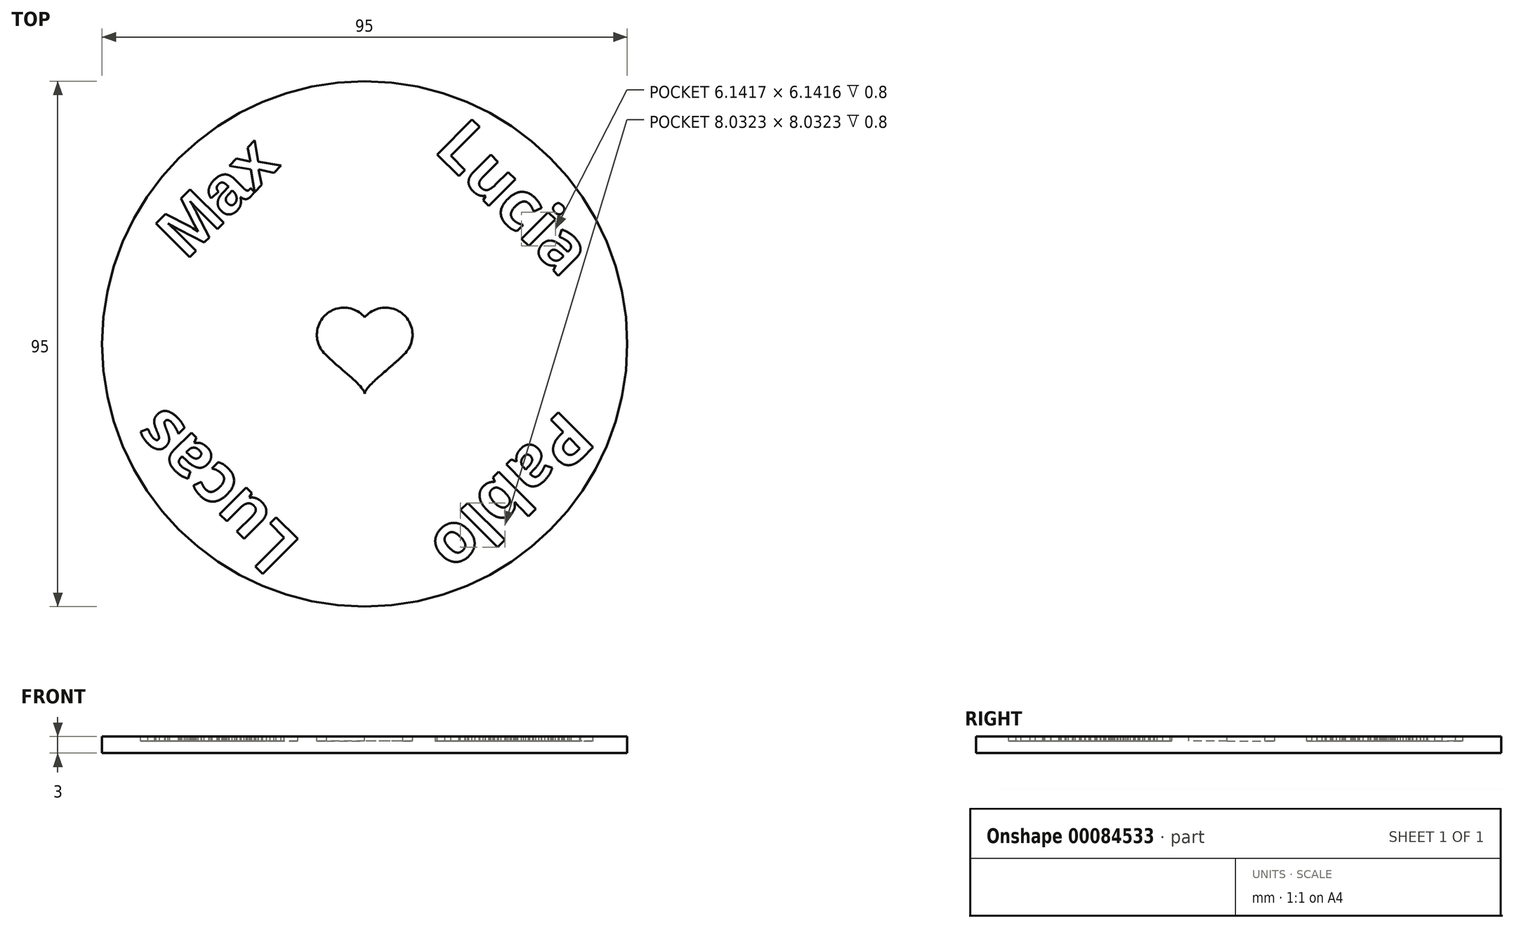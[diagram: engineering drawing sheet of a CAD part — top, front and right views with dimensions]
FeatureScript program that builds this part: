
annotation { "Feature Type Name" : "Feature", "Feature Type Description" : "" }
export const myFeature = defineFeature(function(context is Context, id is Id, definition is map)
    precondition{}
    {
        {
            var Q0;
            Q0=qCreatedBy(makeId("Top.planeOp"),FACE);
            var sketch = newSketch(context, id + "F0", { "sketchPlane" : qUnion([Q0])});
            skCircle(sketch, "E0", {"center": v(0, 0) * mm, "radius": 47.5 * mm});
            skSolve(sketch);
        }
        {
            var Q0;
            Q0 = qSketchRegion(id + "F0", true);
            extrude(context, id + "F1", {"entities" : qUnion([Q0]), "depth" : 3 * mm});
        }
        {
            var Q0;
            Q0=makeQuery(id+"F1.opExtrude","CAP_FACE",FACE,{"disambiguationData":[OSD([sQuery(id+"F0.wireOp",EDGE,"E0")])],"isStart":false});
            var sketch = newSketch(context, id + "F2", { "sketchPlane" : qUnion([Q0])});
            skText(sketch, "E1", { "text": "Max", "fontName": "Arimo-Bold.ttf"});
            skLineSegment(sketch, "E2", {"start": v(0, 0) * mm, "end": v(-47.5, 0) * mm});
            skText(sketch, "E3", { "text": "Lucia", "fontName": "OpenSans-Bold.ttf"});
            skText(sketch, "E4", { "text": "Lucas", "fontName": "OpenSans-Bold.ttf"});
            skLineSegment(sketch, "E5", {"start": v(0, -9) * mm, "end": v(0, 4.8) * mm});
            skPoint(sketch, "E6.startSnap0", {"position": v(0, 0) * mm});
            skArc(sketch, "E7", {"start": v(6.9, -2.1) * mm, "mid": v(7.22, 5.12) * mm, "end": v(0, 4.8) * mm});
            skFitSpline(sketch, "E8", {"points": [v(6.9, -2.1) * mm, v(0, -9) * mm], "startDerivative": vector(-6.9, -6.9) * mm, "endDerivative": vector(0, -3.8) * mm});
            skFitSpline(sketch, "E9.MirrorCS", {"points": [v(-6.9, -2.1) * mm, v(0, -9) * mm], "startDerivative": vector(6.9, -6.9) * mm, "endDerivative": vector(0, -3.8) * mm});
            skArc(sketch, "E10.MirrorCS", {"start": v(-6.9, -2.1) * mm, "mid": v(-7.22, 5.12) * mm, "end": v(0, 4.8) * mm});
            skPoint(sketch, "E11.orphan", {"position": v(-33.59, 33.59) * mm});
            skPoint(sketch, "E12.end.orphan", {"position": v(-33.59, -33.59) * mm});
            skPoint(sketch, "E13.end.orphan", {"position": v(33.59, 33.59) * mm});
            skLineSegment(sketch, "E14", {"start": v(0, 0) * mm, "end": v(4.38, -4.38) * mm});
            skText(sketch, "E15", { "text": "Pablo", "fontName": "OpenSans-Bold.ttf"});
            skPoint(sketch, "E16.orphan", {"position": v(33.59, -33.59) * mm});
            const initialGuessF2  = {"E1": [-0.03225, 0.01512, 0.7071, 0.7071, 0.009], "E3": [0.01233, 0.03505, 0.7071, -0.7071, 0.009], "E4": [-0.01132, -0.03606, -0.7071, 0.7071, 0.009], "E15": [0.03582, -0.01156, -0.7071, -0.7071, 0.009]};
            skSetInitialGuess(sketch, initialGuessF2);
            skSolve(sketch);
        }
        {
            var Q0;
            Q0 = qSketchRegion(id + "F2", true);
            extrude(context, id + "F3", {"entities" : qUnion([Q0]), "operationType" : NewBodyOperationType.REMOVE, "oppositeDirection" : true, "depth" : 0.8 * mm});
        }
    });
